# Revit family: E_Cable Tray Support_MEPcontent_OBO Bettermann_Bracket TPSA FT
name_source: partatom
category: Cable Tray Fittings
revit_build: Autodesk Revit MEP 2015 (Build: 20140606_1530(x64)
units: mm (PartAtom-declared; Revit-internal decimal feet)

## types (4) — shared parameters
Article Description = Wall and Ceiling Bracket
Depth = 60 mm  [stored 0.19685 ft]
Description = Wall and Ceiling Bracket
EMCS Version = 2.0
ETIM Article Class = EC000022
Family Version = 10.14
Gray = Color RGB 189-187-185
Height = 120 mm
Height 1 = 120 mm  [stored 0.393701 ft]
IFCExportAs = IfcCableCarrierFittingType
IFCExportType = NOTDEFINED
MEPcontent Class = CABLE_TRAY_SUPPORT
Manufacturer = OBO BETTERMANN
Manufacturer URL = http://catalog4.obo-bettermann.com
Product Line = OBO BETTERMANN CableTrays
Revit Version = 2015
URL = www.stabiplan.com

## per-type parameters (varying)
| type | GTIN | Manufacturer Art. No. | Width | Width 1 |
| TPSA 145 FT | 4012196473892 | 6364659 | 145 mm | 145 mm  [stored 0.475722 ft] |
| TPSA 245 FT | 4012196473953 | 6364667 | 245 mm | 245 mm  [stored 0.803806 ft] |
| TPSA 345 FT | 4012196474011 | 6364675 | 345 mm | 345 mm  [stored 1.13189 ft] |
| TPSA 195 FT | 4012196555673 | 6364683 | 195 mm | 195 mm  [stored 0.639764 ft] |

note: column(s) folded — value = type name in every type: Article Type, Model

note: [stored X ft] marks values corroborated as IEEE doubles in the binary element streams (Revit-internal decimal feet)

## geometry (parser evidence)
native form markers: Blend x4, Sweep x3
no freeform markers — native parametric forms only
